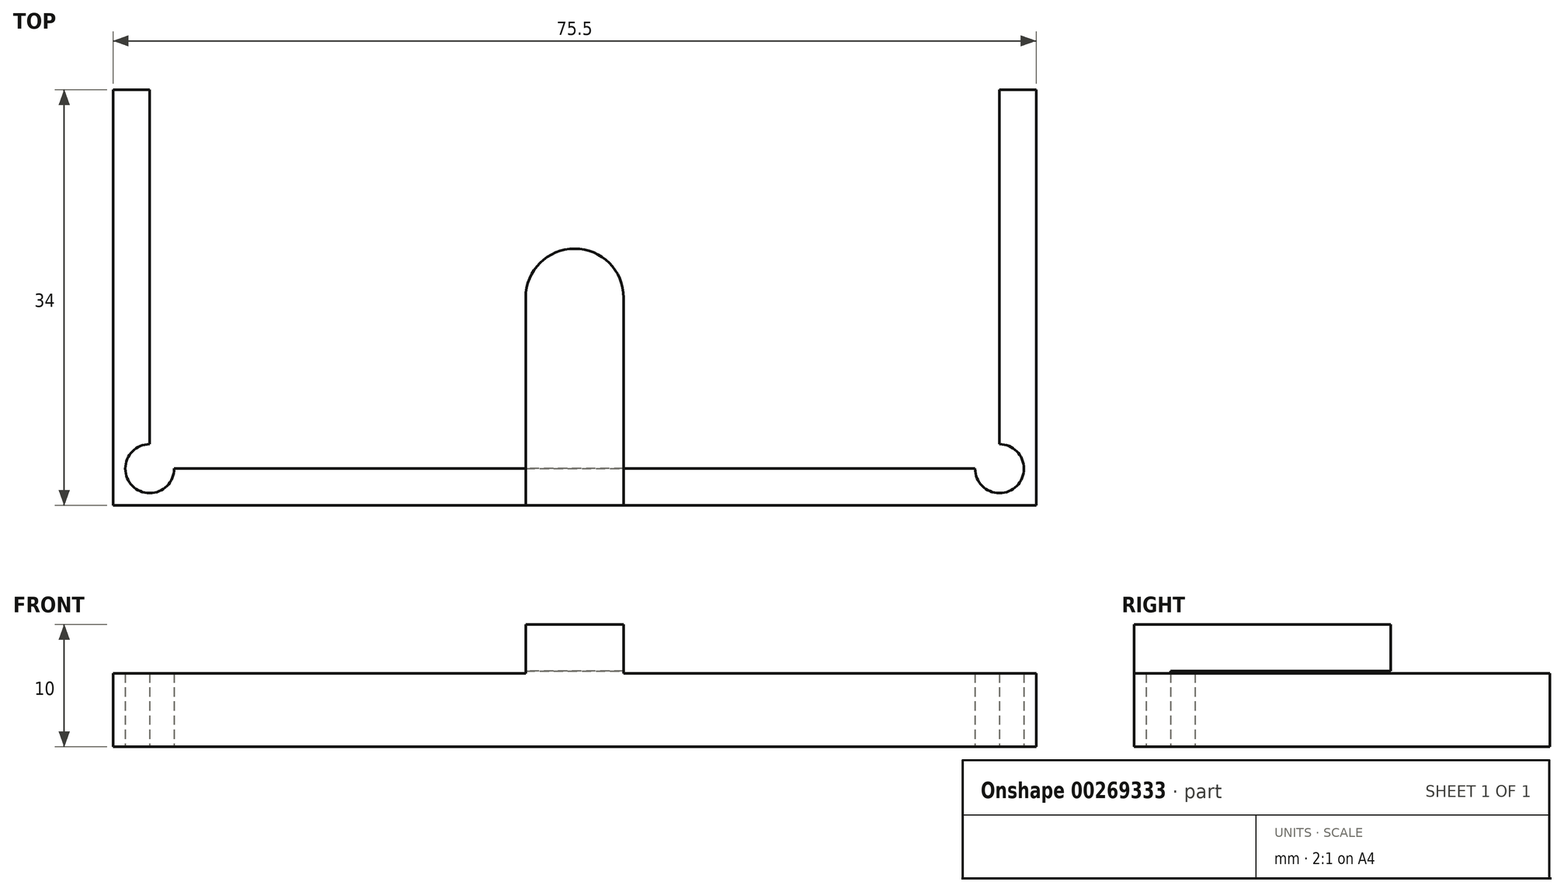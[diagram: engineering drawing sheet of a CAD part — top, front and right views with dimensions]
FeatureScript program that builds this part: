
annotation { "Feature Type Name" : "Feature", "Feature Type Description" : "" }
export const myFeature = defineFeature(function(context is Context, id is Id, definition is map)
    precondition{}
    {
        {
            var Q0;
            Q0=qCreatedBy(makeId("Front.planeOp"),FACE);
            var sketch = newSketch(context, id + "F0", { "sketchPlane" : qUnion([Q0])});
            skLineSegment(sketch, "E0", {"start": v(-37.75, 0) * mm, "end": v(37.75, 0) * mm});
            skLineSegment(sketch, "E1", {"start": v(37.75, 0) * mm, "end": v(37.75, -10) * mm});
            skLineSegment(sketch, "E2", {"start": v(37.75, -10) * mm, "end": v(34.75, -10) * mm});
            skLineSegment(sketch, "E3", {"start": v(34.75, -10) * mm, "end": v(34.75, -4) * mm});
            skLineSegment(sketch, "E4", {"start": v(34.75, -4) * mm, "end": v(5, -4) * mm});
            skLineSegment(sketch, "E5", {"start": v(-34.75, -4) * mm, "end": v(-34.75, -10) * mm});
            skLineSegment(sketch, "E6", {"start": v(-34.75, -10) * mm, "end": v(-37.75, -10) * mm});
            skLineSegment(sketch, "E7", {"start": v(-37.75, -10) * mm, "end": v(-37.75, 0) * mm});
            skLineSegment(sketch, "E8", {"start": v(-5, -4) * mm, "end": v(-5, -3.8) * mm});
            skLineSegment(sketch, "E9", {"start": v(-5, -3.8) * mm, "end": v(5, -3.8) * mm});
            skLineSegment(sketch, "E10", {"start": v(5, -3.8) * mm, "end": v(5, -4) * mm});
            skLineSegment(sketch, "E11.trimOffspring", {"start": v(-5, -4) * mm, "end": v(-34.75, -4) * mm});
            skLineSegment(sketch, "E12", {"start": v(0, 0) * mm, "end": v(0, -3.8) * mm, "construction": true});
            skSolve(sketch);
        }
        {
            var Q0;
            Q0=makeQuery(id+"F0.imprint","IMPRINT",FACE,{"disambiguationData":[TD([[makeQuery(id+"F0.imprint","IMPRINT",EDGE,{"derivedFrom":sQuery(id+"F0.wireOp",EDGE,"E0")}),-1.0]])]});
            extrude(context, id + "F1", {"entities" : qUnion([Q0]), "depth" : 31 * mm});
        }
        {
            var Q0;
            Q0=makeQuery(id+"F1.opExtrude","CAP_FACE",FACE,{"disambiguationData":[OSD([sQuery(id+"F0.wireOp",EDGE,"E0"),sQuery(id+"F0.wireOp",EDGE,"E1"),sQuery(id+"F0.wireOp",EDGE,"E2"),sQuery(id+"F0.wireOp",EDGE,"E3"),sQuery(id+"F0.wireOp",EDGE,"E4"),sQuery(id+"F0.wireOp",EDGE,"E5"),sQuery(id+"F0.wireOp",EDGE,"E6"),sQuery(id+"F0.wireOp",EDGE,"E7"),sQuery(id+"F0.wireOp",EDGE,"E8"),sQuery(id+"F0.wireOp",EDGE,"E9"),sQuery(id+"F0.wireOp",EDGE,"E10"),sQuery(id+"F0.wireOp",EDGE,"E11.trimOffspring")])],"isStart":false});
            var sketch = newSketch(context, id + "F2", { "sketchPlane" : qUnion([Q0])});
            skLineSegment(sketch, "E13.bottom", {"start": v(-37.75, 0) * mm, "end": v(37.75, 0) * mm});
            skLineSegment(sketch, "E13.top", {"start": v(-37.75, -10) * mm, "end": v(37.75, -10) * mm});
            skLineSegment(sketch, "E13.left", {"start": v(-37.75, 0) * mm, "end": v(-37.75, -10) * mm});
            skLineSegment(sketch, "E13.right", {"start": v(37.75, 0) * mm, "end": v(37.75, -10) * mm});
            skSolve(sketch);
        }
        {
            var Q0;
            {var subQ2=sQuery(id+"F2.wireOp",EDGE,"E13.right");Q0=makeQuery(id+"F2.imprint","IMPRINT",FACE,{"disambiguationData":[TD([[makeQuery(id+"F2.imprint","IMPRINT",EDGE,{"derivedFrom":subQ2}),-1.0]])]});}
            var Q1;
            {var subQ3=sQuery(id+"F2.wireOp",EDGE,"E13.left");Q1=makeQuery(id+"F2.imprint","IMPRINT",FACE,{"disambiguationData":[TD([[makeQuery(id+"F2.imprint","IMPRINT",EDGE,{"derivedFrom":subQ3}),-1.0]])]});}
            var Q2;
            {var subQ6=sQuery(id+"F0.wireOp",EDGE,"E3");var subQ7=makeQuery(id+"F1.opExtrude","CAP_EDGE",EDGE,{"disambiguationData":[OSD([subQ6])],"isStart":false});Q2=makeQuery(id+"F2.imprint","IMPRINT",FACE,{"disambiguationData":[TD([[makeQuery(id+"F2.imprint","IMPRINT",EDGE,{"derivedFrom":subQ7}),1.0]])]});}
            extrude(context, id + "F3", {"entities" : qUnion([Q0, Q1, Q2]), "operationType" : NewBodyOperationType.ADD, "depth" : 3 * mm});
        }
        {
            var Q0;
            Q0=makeQuery(id+"F1.opExtrude","SWEPT_FACE",FACE,{"disambiguationData":[OSD([sQuery(id+"F0.wireOp",EDGE,"E0")])]});
            var sketch = newSketch(context, id + "F4", { "sketchPlane" : qUnion([Q0])});
            skLineSegment(sketch, "E14", {"start": v(-15.5, 0) * mm, "end": v(-15.5, -3) * mm});
            skLineSegment(sketch, "E15", {"start": v(-15.5, -3) * mm, "end": v(-5, -3) * mm});
            skLineSegment(sketch, "E16", {"start": v(15.5, -3) * mm, "end": v(15.5, 0) * mm});
            skLineSegment(sketch, "E17", {"start": v(0, 0) * mm, "end": v(0, -34) * mm, "construction": true});
            skLineSegment(sketch, "E18", {"start": v(-5, -3) * mm, "end": v(-5, -8) * mm});
            skLineSegment(sketch, "E19", {"start": v(5, -3) * mm, "end": v(5, -8) * mm});
            skLineSegment(sketch, "E20.trimOffspring", {"start": v(5, -3) * mm, "end": v(15.5, -3) * mm});
            skLineSegment(sketch, "E21", {"start": v(-5, -8) * mm, "end": v(5, -8) * mm});
            skArc(sketch, "E22", {"start": v(-4, -17) * mm, "mid": v(0, -13) * mm, "end": v(4, -17) * mm});
            skLineSegment(sketch, "E23.trimOffspring", {"start": v(4, -17) * mm, "end": v(4, -34) * mm});
            skLineSegment(sketch, "E24.trimOffspring", {"start": v(-4, -17) * mm, "end": v(-4, -34) * mm});
            skLineSegment(sketch, "E25", {"start": v(-4, -34) * mm, "end": v(4, -34) * mm});
            skSolve(sketch);
        }
        {
            var Q0;
            Q0=makeQuery(id+"F4.imprint","IMPRINT",FACE,{"disambiguationData":[TD([[makeQuery(id+"F4.imprint","IMPRINT",EDGE,{"derivedFrom":sQuery(id+"F4.wireOp",EDGE,"E22")}),-1.0]])]});
            var Q1;
            {var subQ1=sQuery(id+"F4.wireOp",EDGE,"E14");Q1=makeQuery(id+"F4.imprint","IMPRINT",FACE,{"disambiguationData":[TD([[makeQuery(id+"F4.imprint","IMPRINT",EDGE,{"derivedFrom":subQ1}),1.0]])]});}
            extrude(context, id + "F5", {"entities" : qUnion([Q0, Q1]), "operationType" : NewBodyOperationType.REMOVE, "oppositeDirection" : true, "depth" : 4 * mm});
        }
        {
            var Q0;
            Q0=makeQuery(id+"F1.opExtrude","SWEPT_FACE",FACE,{"disambiguationData":[OSD([sQuery(id+"F0.wireOp",EDGE,"E0")])]});
            var sketch = newSketch(context, id + "F6", { "sketchPlane" : qUnion([Q0])});
            skLineSegment(sketch, "E26.bottom", {"start": v(-7, -34) * mm, "end": v(7, -34) * mm});
            skLineSegment(sketch, "E26.left", {"start": v(-7, -34) * mm, "end": v(-7, -17) * mm});
            skLineSegment(sketch, "E26.right", {"start": v(7, -34) * mm, "end": v(7, -17) * mm});
            skLineSegment(sketch, "E27", {"start": v(0, -10) * mm, "end": v(0, -34) * mm, "construction": true});
            skArc(sketch, "E28", {"start": v(-7, -17) * mm, "mid": v(0, -10) * mm, "end": v(7, -17) * mm});
            skSolve(sketch);
        }
        {
            var Q0;
            Q0=makeQuery(id+"F6.imprint","IMPRINT",FACE,{"disambiguationData":[TD([[makeQuery(id+"F6.imprint","IMPRINT",EDGE,{"derivedFrom":sQuery(id+"F6.wireOp",EDGE,"E26.bottom")}),1.0]])]});
            extrude(context, id + "F7", {"entities" : qUnion([Q0]), "operationType" : NewBodyOperationType.REMOVE, "oppositeDirection" : true, "depth" : 3.2 * mm});
        }
        {
            var Q0;
            Q0=makeQuery(id+"F3.boolean.opBoolean","MERGE",FACE,{"derivedFrom":[makeQuery(id+"F1.opExtrude","SWEPT_FACE",FACE,{"disambiguationData":[OSD([sQuery(id+"F0.wireOp",EDGE,"E2")])]}),makeQuery(id+"F1.opExtrude","SWEPT_FACE",FACE,{"disambiguationData":[OSD([sQuery(id+"F0.wireOp",EDGE,"E6")])]}),makeQuery(id+"F3.opExtrude","SWEPT_FACE",FACE,{"disambiguationData":[OSD([sQuery(id+"F2.wireOp",EDGE,"E13.top")])]})]});
            var sketch = newSketch(context, id + "F8", { "sketchPlane" : qUnion([Q0])});
            skCircle(sketch, "E29", {"center": v(-34.75, 31) * mm, "radius": 2 * mm});
            skCircle(sketch, "E30", {"center": v(34.75, 31) * mm, "radius": 2 * mm});
            skCircle(sketch, "E31", {"center": v(-5, 31) * mm, "radius": 1.5 * mm});
            skCircle(sketch, "E32", {"center": v(5, 31) * mm, "radius": 1.5 * mm});
            skSolve(sketch);
        }
        {
            var Q0;
            {var subQ0=sQuery(id+"F8.wireOp",EDGE,"E29");var subQ3=makeQuery(id+"F3.opExtrude","CAP_EDGE",EDGE,{"disambiguationData":[OSD([sQuery(id+"F2.wireOp",EDGE,"E13.top")])],"isStart":true});var subQ4=makeQuery(id+"F8.imprint","INTERSECT",VERTEX,{"derivedFrom":[subQ3,subQ0]});Q0=makeQuery(id+"F8.imprint","IMPRINT",FACE,{"disambiguationData":[TD([[makeQuery(id+"F8.imprint","IMPRINT",EDGE,{"disambiguationData":[TD([[subQ4,-1.0]])],"derivedFrom":subQ0}),1.0]])]});}
            var Q1;
            {var subQ0=sQuery(id+"F8.wireOp",EDGE,"E29");var subQ3=makeQuery(id+"F3.opExtrude","CAP_EDGE",EDGE,{"disambiguationData":[OSD([sQuery(id+"F2.wireOp",EDGE,"E13.top")])],"isStart":true});var subQ4=makeQuery(id+"F8.imprint","INTERSECT",VERTEX,{"derivedFrom":[subQ3,subQ0]});Q1=makeQuery(id+"F8.imprint","IMPRINT",FACE,{"disambiguationData":[TD([[makeQuery(id+"F8.imprint","IMPRINT",EDGE,{"disambiguationData":[TD([[subQ4,1.0]])],"derivedFrom":subQ0}),1.0]])]});}
            var Q2;
            {var subQ0=sQuery(id+"F8.wireOp",EDGE,"E30");var subQ3=makeQuery(id+"F3.opExtrude","CAP_EDGE",EDGE,{"disambiguationData":[OSD([sQuery(id+"F2.wireOp",EDGE,"E13.top")])],"isStart":true});var subQ4=makeQuery(id+"F8.imprint","INTERSECT",VERTEX,{"derivedFrom":[subQ3,subQ0]});Q2=makeQuery(id+"F8.imprint","IMPRINT",FACE,{"disambiguationData":[TD([[makeQuery(id+"F8.imprint","IMPRINT",EDGE,{"disambiguationData":[TD([[subQ4,1.0]])],"derivedFrom":subQ0}),1.0]])]});}
            var Q3;
            {var subQ0=sQuery(id+"F8.wireOp",EDGE,"E30");var subQ3=makeQuery(id+"F3.opExtrude","CAP_EDGE",EDGE,{"disambiguationData":[OSD([sQuery(id+"F2.wireOp",EDGE,"E13.top")])],"isStart":true});var subQ4=makeQuery(id+"F8.imprint","INTERSECT",VERTEX,{"derivedFrom":[subQ3,subQ0]});Q3=makeQuery(id+"F8.imprint","IMPRINT",FACE,{"disambiguationData":[TD([[makeQuery(id+"F8.imprint","IMPRINT",EDGE,{"disambiguationData":[TD([[subQ4,-1.0]])],"derivedFrom":subQ0}),1.0]])]});}
            extrude(context, id + "F9", {"entities" : qUnion([Q0, Q1, Q2, Q3]), "operationType" : NewBodyOperationType.REMOVE, "oppositeDirection" : true, "depth" : 7 * mm});
        }
    });
